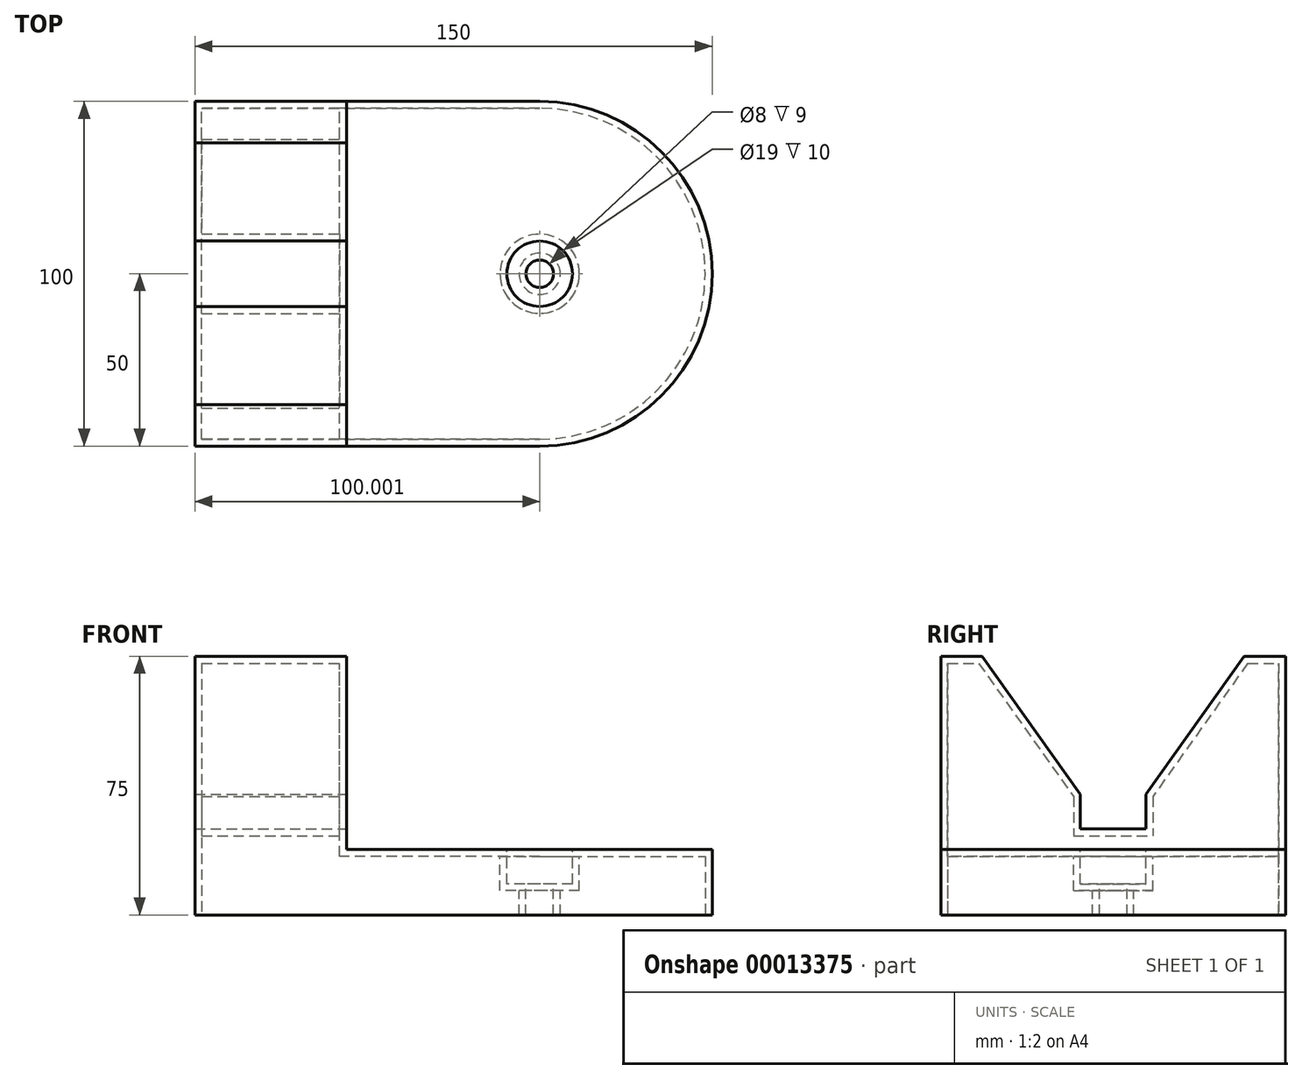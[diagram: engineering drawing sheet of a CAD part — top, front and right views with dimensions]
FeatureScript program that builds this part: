
annotation { "Feature Type Name" : "Feature", "Feature Type Description" : "" }
export const myFeature = defineFeature(function(context is Context, id is Id, definition is map)
    precondition{}
    {
        {
            var Q0;
            Q0=qCreatedBy(makeId("Front.planeOp"),FACE);
            var sketch = newSketch(context, id + "F0", { "sketchPlane" : qUnion([Q0])});
            skLineSegment(sketch, "E0", {"start": v(-55.35, 53) * mm, "end": v(-55.35, -22) * mm});
            skLineSegment(sketch, "E1", {"start": v(-55.35, -22) * mm, "end": v(94.65, -22) * mm});
            skLineSegment(sketch, "E2", {"start": v(94.65, -22) * mm, "end": v(94.65, -3) * mm});
            skLineSegment(sketch, "E3", {"start": v(94.65, -3) * mm, "end": v(-11.35, -3) * mm});
            skLineSegment(sketch, "E4", {"start": v(-11.35, -3) * mm, "end": v(-11.35, 53) * mm});
            skLineSegment(sketch, "E5", {"start": v(-11.35, 53) * mm, "end": v(-55.35, 53) * mm});
            skSolve(sketch);
        }
        {
            var Q0;
            Q0=makeQuery(id+"F0.imprint","IMPRINT",FACE,{"disambiguationData":[TD([[makeQuery(id+"F0.imprint","IMPRINT",EDGE,{"derivedFrom":sQuery(id+"F0.wireOp",EDGE,"E0")}),1.0]])]});
            extrude(context, id + "F1", {"entities" : qUnion([Q0]), "depth" : 100 * mm, "symmetric" : true});
        }
        {
            var Q0;
            Q0=qCreatedBy(makeId("Right.planeOp"),FACE);
            var sketch = newSketch(context, id + "F2", { "sketchPlane" : qUnion([Q0])});
            skLineSegment(sketch, "E6.bottom", {"start": v(-9.5, 61.94) * mm, "end": v(9.5, 61.94) * mm});
            skLineSegment(sketch, "E6.top", {"start": v(-9.5, 3) * mm, "end": v(9.5, 3) * mm});
            skLineSegment(sketch, "E6.left", {"start": v(-9.5, 61.94) * mm, "end": v(-9.5, 3) * mm});
            skLineSegment(sketch, "E6.right", {"start": v(9.5, 61.94) * mm, "end": v(9.5, 3) * mm});
            skLineSegment(sketch, "E7.top", {"start": v(-9.5, 13) * mm, "end": v(9.5, 13) * mm});
            skLineSegment(sketch, "E8", {"start": v(38, 53) * mm, "end": v(-38, 53) * mm});
            skLineSegment(sketch, "E9", {"start": v(-38, 53) * mm, "end": v(-9.5, 13) * mm});
            skLineSegment(sketch, "E10", {"start": v(38, 53) * mm, "end": v(9.5, 13) * mm});
            skSolve(sketch);
        }
        {
            var Q0;
            {var subQ0=sQuery(id+"F2.wireOp",EDGE,"E9");Q0=makeQuery(id+"F2.imprint","IMPRINT",FACE,{"disambiguationData":[TD([[makeQuery(id+"F2.imprint","IMPRINT",EDGE,{"derivedFrom":subQ0}),1.0]])]});}
            var Q1;
            {var subQ0=sQuery(id+"F2.wireOp",EDGE,"E10");Q1=makeQuery(id+"F2.imprint","IMPRINT",FACE,{"disambiguationData":[TD([[makeQuery(id+"F2.imprint","IMPRINT",EDGE,{"derivedFrom":subQ0}),-1.0]])]});}
            var Q2;
            {var subQ0=sQuery(id+"F2.wireOp",EDGE,"E7.top");Q2=makeQuery(id+"F2.imprint","IMPRINT",FACE,{"disambiguationData":[TD([[makeQuery(id+"F2.imprint","IMPRINT",EDGE,{"derivedFrom":subQ0}),1.0]])]});}
            var Q3;
            {var subQ0=sQuery(id+"F2.wireOp",EDGE,"E6.top");Q3=makeQuery(id+"F2.imprint","IMPRINT",FACE,{"disambiguationData":[TD([[makeQuery(id+"F2.imprint","IMPRINT",EDGE,{"derivedFrom":subQ0}),1.0]])]});}
            extrude(context, id + "F3", {"entities" : qUnion([Q0, Q1, Q2, Q3]), "operationType" : NewBodyOperationType.REMOVE, "endBound" : BoundingType.THROUGH_ALL, "oppositeDirection" : true, "depth" : 25 * mm});
        }
        {
            var Q0;
            Q0=makeQuery(id+"F1.opExtrude","SWEPT_FACE",FACE,{"disambiguationData":[OSD([sQuery(id+"F0.wireOp",EDGE,"E1")])]});
            var sketch = newSketch(context, id + "F4", { "sketchPlane" : qUnion([Q0])});
            skArc(sketch, "E11", {"start": v(44.65, -50) * mm, "mid": v(94.65, 0) * mm, "end": v(44.65, 50) * mm});
            skPoint(sketch, "E11.first.point", {"position": v(44.65, 50) * mm});
            skPoint(sketch, "E11.second.point", {"position": v(94.65, 0) * mm});
            skPoint(sketch, "E11.third.point", {"position": v(44.65, -50) * mm});
            skSolve(sketch);
        }
        {
            var Q0;
            {var subQ0=sQuery(id+"F4.wireOp",EDGE,"E11");var subQ1=sQuery(id+"F0.wireOp",EDGE,"E1");var subQ4=makeQuery(id+"F1.opExtrude","CAP_EDGE",EDGE,{"disambiguationData":[OSD([subQ1])],"isStart":false});var subQ5=makeQuery(id+"F4.imprint","INTERSECT",VERTEX,{"disambiguationData":[OD(1.0)],"derivedFrom":[subQ4,subQ0]});Q0=makeQuery(id+"F4.imprint","IMPRINT",FACE,{"disambiguationData":[TD([[makeQuery(id+"F4.imprint","IMPRINT",EDGE,{"disambiguationData":[TD([[subQ5,1.0]])],"derivedFrom":subQ0}),-1.0]])]});}
            var Q1;
            {var subQ0=sQuery(id+"F4.wireOp",EDGE,"E11");var subQ1=sQuery(id+"F0.wireOp",EDGE,"E1");var subQ2=makeQuery(id+"F1.opExtrude","CAP_EDGE",EDGE,{"disambiguationData":[OSD([subQ1])],"isStart":true});var subQ3=makeQuery(id+"F4.imprint","INTERSECT",VERTEX,{"derivedFrom":[subQ2,subQ0]});Q1=makeQuery(id+"F4.imprint","IMPRINT",FACE,{"disambiguationData":[TD([[makeQuery(id+"F4.imprint","IMPRINT",EDGE,{"disambiguationData":[TD([[subQ3,-1.0]])],"derivedFrom":subQ0}),-1.0]])]});}
            extrude(context, id + "F5", {"entities" : qUnion([Q0, Q1]), "operationType" : NewBodyOperationType.REMOVE, "endBound" : BoundingType.THROUGH_ALL, "oppositeDirection" : true, "depth" : 25 * mm});
        }
        {
            var Q0;
            Q0=makeQuery(id+"F1.opExtrude","SWEPT_FACE",FACE,{"disambiguationData":[OSD([sQuery(id+"F0.wireOp",EDGE,"E3")])]});
            var sketch = newSketch(context, id + "F6", { "sketchPlane" : qUnion([Q0])});
            skCircle(sketch, "E12", {"center": v(44.65, 0) * mm, "radius": 4 * mm});
            skCircle(sketch, "E13", {"center": v(44.65, 0) * mm, "radius": 9.5 * mm});
            skSolve(sketch);
        }
        {
            var Q0;
            Q0=makeQuery(id+"F6.imprint","IMPRINT",FACE,{"disambiguationData":[TD([[makeQuery(id+"F6.imprint","IMPRINT",EDGE,{"derivedFrom":sQuery(id+"F6.wireOp",EDGE,"E12")}),1.0]])]});
            extrude(context, id + "F7", {"entities" : qUnion([Q0]), "operationType" : NewBodyOperationType.REMOVE, "endBound" : BoundingType.THROUGH_ALL, "oppositeDirection" : true, "depth" : 25 * mm});
        }
        {
            var Q0;
            Q0=makeQuery(id+"F6.imprint","IMPRINT",FACE,{"disambiguationData":[TD([[makeQuery(id+"F6.imprint","IMPRINT",EDGE,{"derivedFrom":sQuery(id+"F6.wireOp",EDGE,"E12")}),-1.0]])]});
            extrude(context, id + "F8", {"entities" : qUnion([Q0]), "operationType" : NewBodyOperationType.REMOVE, "oppositeDirection" : true, "depth" : 10 * mm});
        }
        {
            var Q0;
            Q0=makeQuery(id+"F1.opExtrude","SWEPT_FACE",FACE,{"disambiguationData":[OSD([sQuery(id+"F0.wireOp",EDGE,"E1")])]});
            shell(context, id + "F9", {"entities" : qUnion([Q0]), "thickness" : 2 * mm});
        }
    });
